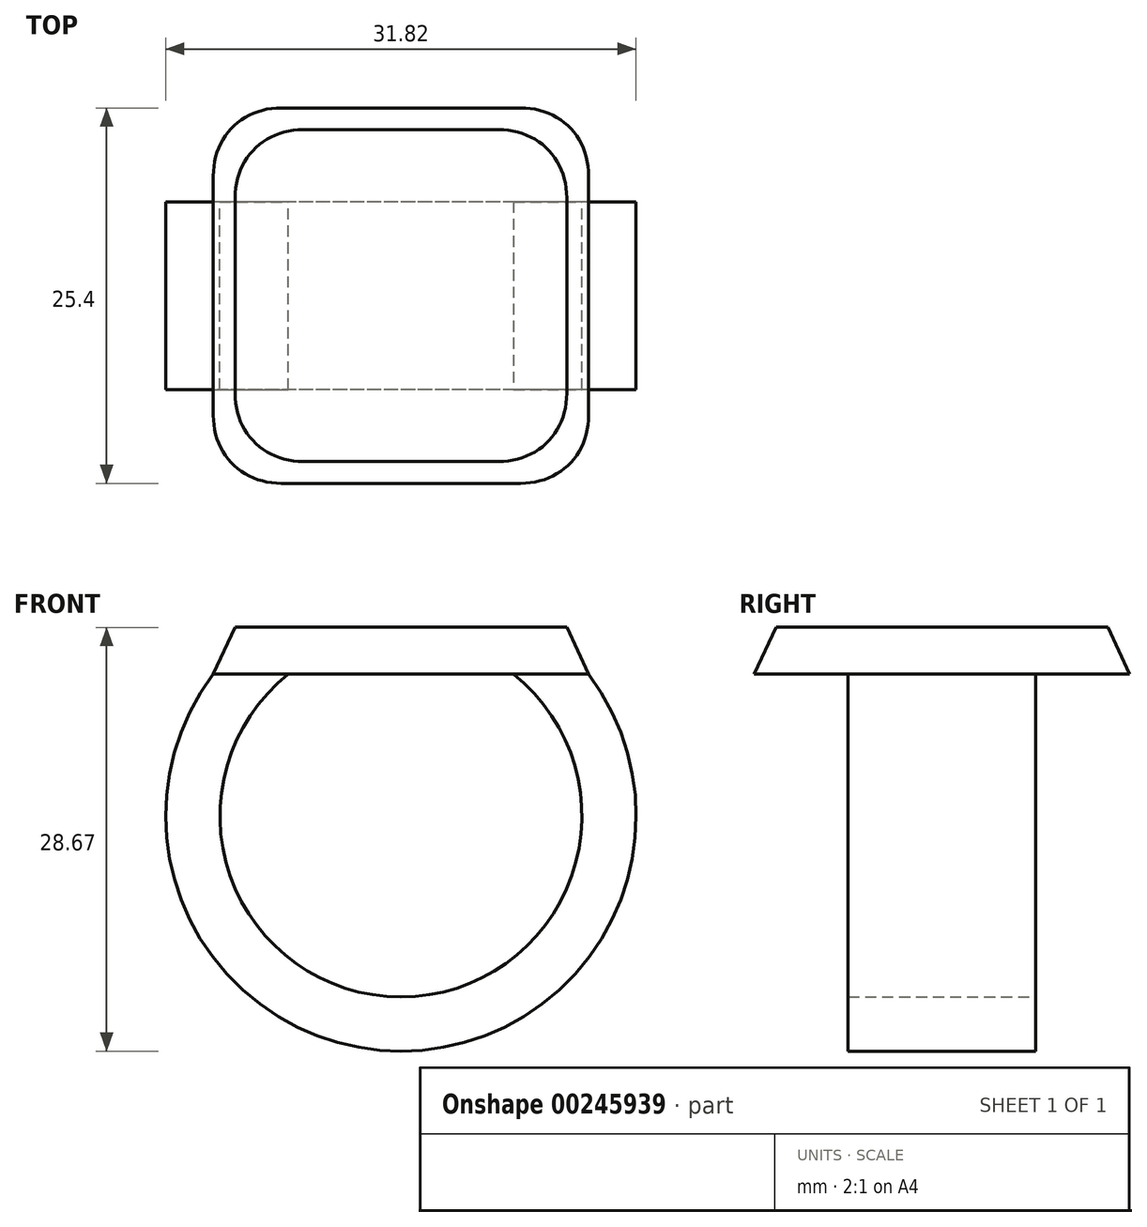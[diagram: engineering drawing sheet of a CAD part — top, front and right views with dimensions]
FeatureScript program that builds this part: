
annotation { "Feature Type Name" : "Feature", "Feature Type Description" : "" }
export const myFeature = defineFeature(function(context is Context, id is Id, definition is map)
    precondition{}
    {
        {
            var Q0;
            Q0=qCreatedBy(makeId("Top.planeOp"),FACE);
            var sketch = newSketch(context, id + "F0", { "sketchPlane" : qUnion([Q0])});
            skLineSegment(sketch, "E0.bottom", {"start": v(12.7, -12.7) * mm, "end": v(-12.7, -12.7) * mm});
            skLineSegment(sketch, "E0.top", {"start": v(12.7, 12.7) * mm, "end": v(-12.7, 12.7) * mm});
            skLineSegment(sketch, "E0.left", {"start": v(12.7, -12.7) * mm, "end": v(12.7, 12.7) * mm});
            skLineSegment(sketch, "E0.right", {"start": v(-12.7, -12.7) * mm, "end": v(-12.7, 12.7) * mm});
            skPoint(sketch, "E0.middle", {"position": v(0, 0) * mm});
            skSolve(sketch);
        }
        {
            var Q0;
            Q0 = qSketchRegion(id + "F0", true);
            extrude(context, id + "F1", {"entities" : qUnion([Q0]), "depth" : 3.17 * mm, "hasDraft" : true, "draftAngle" : 25 * degree, "draftPullDirection" : true});
        }
        {
            var Q0;
            Q0=qCreatedBy(makeId("Front.planeOp"),FACE);
            var sketch = newSketch(context, id + "F2", { "sketchPlane" : qUnion([Q0])});
            skArc(sketch, "E1", {"start": v(-10.16, 0) * mm, "mid": v(0, -23.56) * mm, "end": v(10.16, 0) * mm});
            skSolve(sketch);
        }
        {
            var Q0;
            Q0=makeQuery(id+"F1.opExtrude","CAP_FACE",FACE,{"disambiguationData":[OSD([sQuery(id+"F0.wireOp",EDGE,"E0.bottom"),sQuery(id+"F0.wireOp",EDGE,"E0.top"),sQuery(id+"F0.wireOp",EDGE,"E0.left"),sQuery(id+"F0.wireOp",EDGE,"E0.right")])],"isStart":true});
            var sketch = newSketch(context, id + "F3", { "sketchPlane" : qUnion([Q0])});
            skLineSegment(sketch, "E2.bottom", {"start": v(12.7, -6.35) * mm, "end": v(7.62, -6.35) * mm});
            skLineSegment(sketch, "E2.top", {"start": v(12.7, 6.35) * mm, "end": v(7.62, 6.35) * mm});
            skLineSegment(sketch, "E2.left", {"start": v(12.7, -6.35) * mm, "end": v(12.7, 6.35) * mm});
            skLineSegment(sketch, "E2.right", {"start": v(7.62, -6.35) * mm, "end": v(7.62, 6.35) * mm});
            skPoint(sketch, "E2.middle", {"position": v(10.16, 0) * mm});
            skSolve(sketch);
        }
        {
            var Q0;
            Q0 = qSketchRegion(id + "F3", true);
            var Q1;
            Q1 = qConstructionFilter(qBodyType(qCreatedBy(id + "F2" ,EDGE), BodyType.WIRE), ConstructionObject.NO);
            sweep(context, id + "F4", {"operationType" : NewBodyOperationType.ADD, "profiles" : qUnion([Q0]), "path" : qUnion([Q1])});
        }
        {
            var Q0;
            Q0=qCreatedBy(makeId("Front.planeOp"),FACE);
            var sketch = newSketch(context, id + "F5", { "sketchPlane" : qUnion([Q0])});
            skLineSegment(sketch, "E3.0.0", {"start": v(-10.16, 0) * mm, "end": v(-7.62, 0) * mm});
            skLineSegment(sketch, "E4.0", {"start": v(-10.16, 0) * mm, "end": v(-10.01, -2.54) * mm});
            skArc(sketch, "E5", {"start": v(-7.62, 0) * mm, "mid": v(-8.9, -1.18) * mm, "end": v(-10.01, -2.54) * mm});
            skSolve(sketch);
        }
        {
            var Q0;
            Q0 = qSketchRegion(id + "F5", true);
            extrude(context, id + "F6", {"entities" : qUnion([Q0]), "operationType" : NewBodyOperationType.ADD, "endBound" : BoundingType.SYMMETRIC, "depth" : 12.7 * mm});
        }
        {
            var Q0;
            Q0=makeQuery(id+"F1.opExtrude","SWEPT_EDGE",EDGE,{"disambiguationData":[OSD([sQuery(id+"F0.wireOp",EDGE,"E0.top"),sQuery(id+"F0.wireOp",EDGE,"E0.right")])]});
            var Q1;
            Q1=makeQuery(id+"F1.opExtrude","SWEPT_EDGE",EDGE,{"disambiguationData":[OSD([sQuery(id+"F0.wireOp",EDGE,"E0.top"),sQuery(id+"F0.wireOp",EDGE,"E0.left")])]});
            var Q2;
            Q2=makeQuery(id+"F1.opExtrude","SWEPT_EDGE",EDGE,{"disambiguationData":[OSD([sQuery(id+"F0.wireOp",EDGE,"E0.bottom"),sQuery(id+"F0.wireOp",EDGE,"E0.left")])]});
            var Q3;
            Q3=makeQuery(id+"F1.opExtrude","SWEPT_EDGE",EDGE,{"disambiguationData":[OSD([sQuery(id+"F0.wireOp",EDGE,"E0.bottom"),sQuery(id+"F0.wireOp",EDGE,"E0.right")])]});
            fillet(context, id + "F7", {"entities" : qUnion([Q0, Q1, Q2, Q3]), "radius" : 5.08 * mm, "tangentPropagation" : true, "allowEdgeOverflow" : false});
        }
    });
